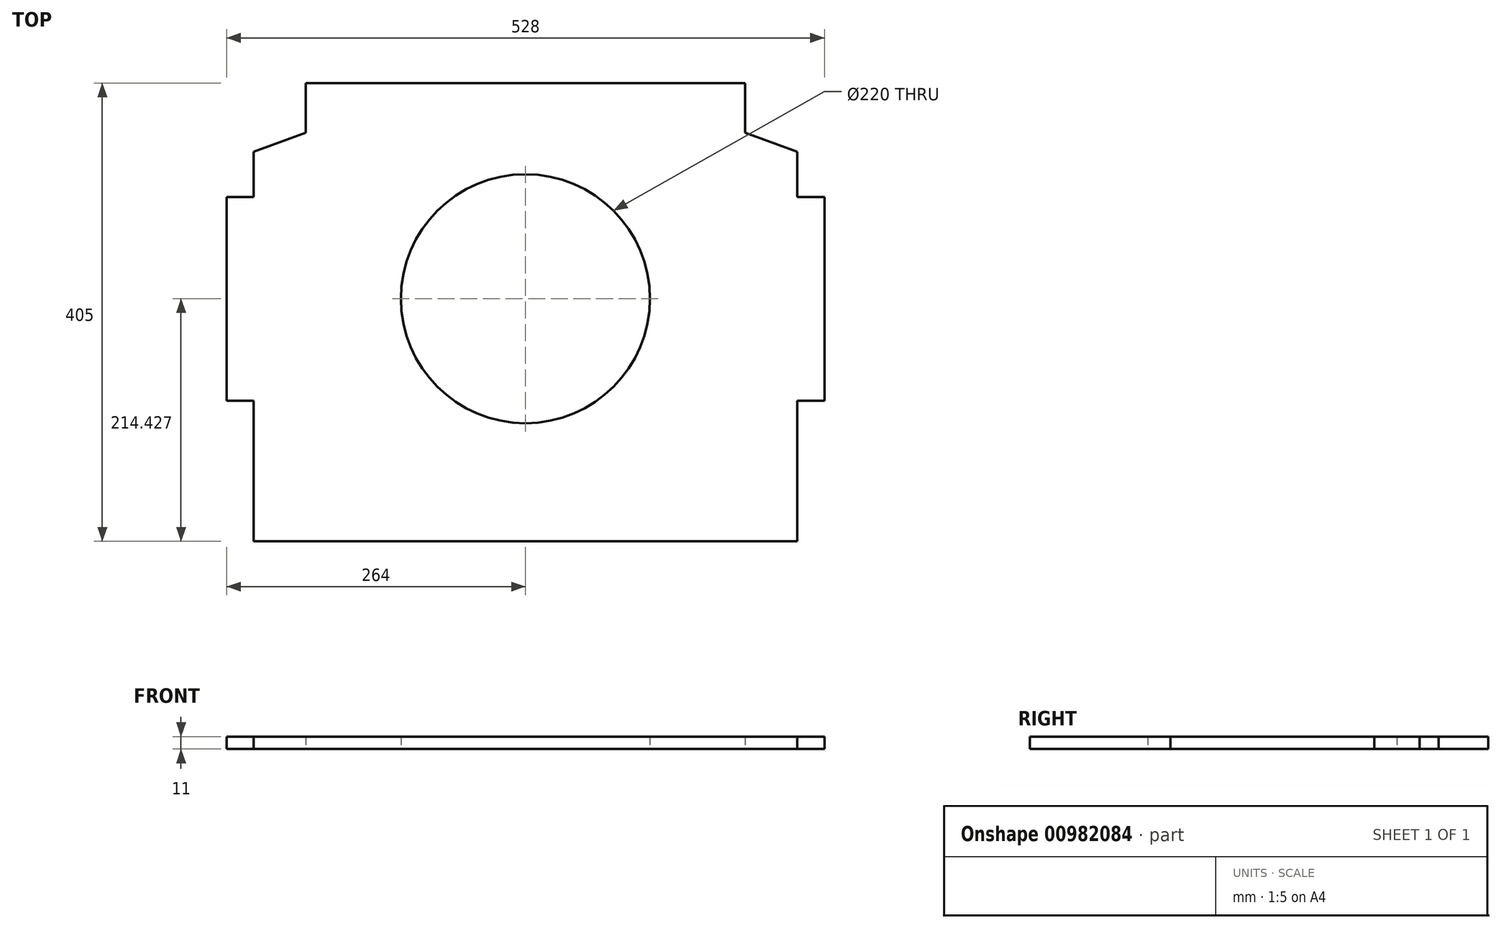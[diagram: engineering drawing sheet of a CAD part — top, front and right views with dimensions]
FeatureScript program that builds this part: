
annotation { "Feature Type Name" : "Feature", "Feature Type Description" : "" }
export const myFeature = defineFeature(function(context is Context, id is Id, definition is map)
    precondition{}
    {
        {
            var Q0;
            Q0=qCreatedBy(makeId("Top.planeOp"),FACE);
            var sketch = newSketch(context, id + "F0", { "sketchPlane" : qUnion([Q0])});
            skLineSegment(sketch, "E0", {"start": v(-194, 158.5) * mm, "end": v(-194, 202.5) * mm});
            skLineSegment(sketch, "E1", {"start": v(194, 158.5) * mm, "end": v(194, 202.5) * mm});
            skCircle(sketch, "E2", {"center": v(0, 11.93) * mm, "radius": 110 * mm});
            skLineSegment(sketch, "E3", {"start": v(240, 101.93) * mm, "end": v(240, 141.93) * mm});
            skLineSegment(sketch, "E4", {"start": v(264, -78.07) * mm, "end": v(264, 101.93) * mm});
            skLineSegment(sketch, "E5", {"start": v(240, 101.93) * mm, "end": v(264, 101.93) * mm});
            skLineSegment(sketch, "E6", {"start": v(194, 158.5) * mm, "end": v(240, 141.93) * mm});
            skLineSegment(sketch, "E7", {"start": v(-240, 101.93) * mm, "end": v(-240, 141.93) * mm});
            skLineSegment(sketch, "E8", {"start": v(-264, -78.07) * mm, "end": v(-264, 101.93) * mm});
            skLineSegment(sketch, "E9", {"start": v(-240, 101.93) * mm, "end": v(-264, 101.93) * mm});
            skLineSegment(sketch, "E10", {"start": v(-194, 158.5) * mm, "end": v(-240, 141.93) * mm});
            skLineSegment(sketch, "E11", {"start": v(-240, -78.07) * mm, "end": v(-264, -78.07) * mm});
            skLineSegment(sketch, "E12", {"start": v(264, -78.07) * mm, "end": v(240, -78.07) * mm});
            skLineSegment(sketch, "E13", {"start": v(-240, -202.5) * mm, "end": v(240, -202.5) * mm});
            skLineSegment(sketch, "E14", {"start": v(-194, 202.5) * mm, "end": v(194, 202.5) * mm});
            skLineSegment(sketch, "E15", {"start": v(-240, -78.07) * mm, "end": v(-240, -202.5) * mm});
            skLineSegment(sketch, "E16", {"start": v(240, -78.07) * mm, "end": v(240, -202.5) * mm});
            skSolve(sketch);
        }
        {
            var Q0;
            Q0=makeQuery(id+"F0.imprint","IMPRINT",FACE,{"disambiguationData":[TD([[makeQuery(id+"F0.imprint","IMPRINT",EDGE,{"derivedFrom":sQuery(id+"F0.wireOp",EDGE,"E0")}),-1.0]])]});
            extrude(context, id + "F1", {"entities" : qUnion([Q0]), "depth" : 11 * mm, "offsetDistance" : 25 * mm});
        }
    });
